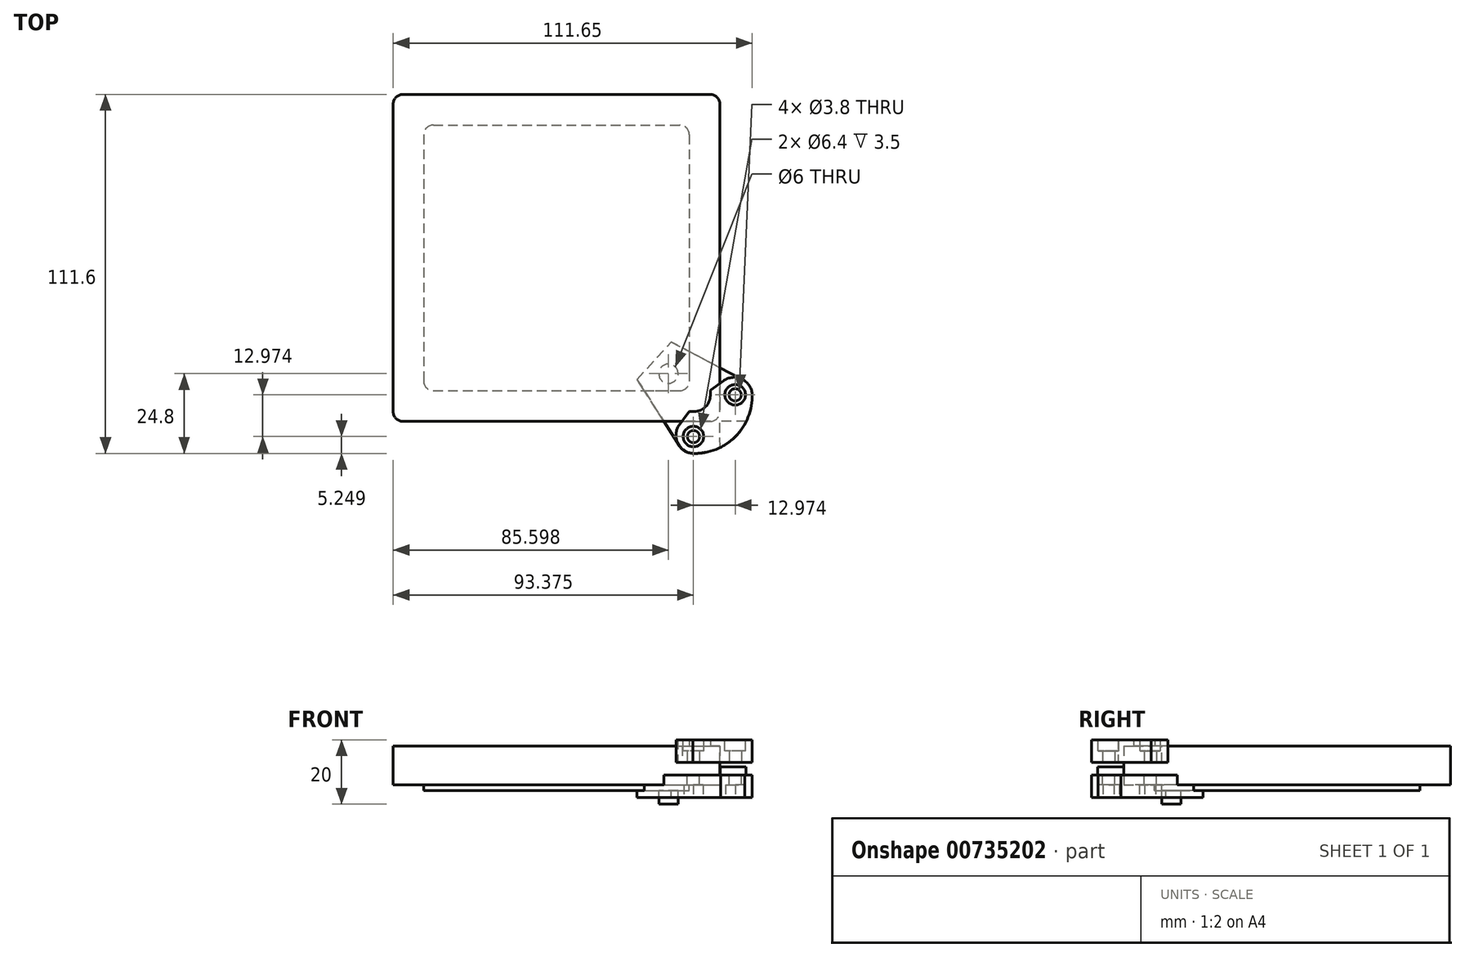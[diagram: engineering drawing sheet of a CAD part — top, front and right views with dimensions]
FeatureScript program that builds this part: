
annotation { "Feature Type Name" : "Feature", "Feature Type Description" : "" }
export const myFeature = defineFeature(function(context is Context, id is Id, definition is map)
    precondition{}
    {
        {
            var Q0;
            Q0=qCreatedBy(makeId("Top.planeOp"),FACE);
            var sketch = newSketch(context, id + "F0", { "sketchPlane" : qUnion([Q0])});
            skLineSegment(sketch, "E0.bottom", {"start": v(-49.2, 52.24) * mm, "end": v(46.4, 52.24) * mm});
            skLineSegment(sketch, "E0.top", {"start": v(-49.2, -49.36) * mm, "end": v(46.4, -49.36) * mm});
            skLineSegment(sketch, "E0.left", {"start": v(-52.2, 49.24) * mm, "end": v(-52.2, -46.36) * mm});
            skLineSegment(sketch, "E0.right", {"start": v(49.4, 49.24) * mm, "end": v(49.4, -46.36) * mm});
            skPoint(sketch, "E1.visualSharp", {"position": v(-52.2, 52.24) * mm});
            skArc(sketch, "E1.filletArc", {"start": v(-49.2, 52.24) * mm, "mid": v(-51.31, 51.36) * mm, "end": v(-52.2, 49.24) * mm});
            skPoint(sketch, "E2.visualSharp", {"position": v(-52.2, -49.36) * mm});
            skArc(sketch, "E2.filletArc", {"start": v(-52.2, -46.36) * mm, "mid": v(-51.31, -48.48) * mm, "end": v(-49.2, -49.36) * mm});
            skPoint(sketch, "E3.visualSharp", {"position": v(49.4, -49.36) * mm});
            skArc(sketch, "E3.filletArc", {"start": v(46.4, -49.36) * mm, "mid": v(48.53, -48.48) * mm, "end": v(49.4, -46.36) * mm});
            skPoint(sketch, "E4.visualSharp", {"position": v(49.4, 52.24) * mm});
            skArc(sketch, "E4.filletArc", {"start": v(49.4, 49.24) * mm, "mid": v(48.53, 51.36) * mm, "end": v(46.4, 52.24) * mm});
            skLineSegment(sketch, "E5.0", {"start": v(-39.7, 42.74) * mm, "end": v(36.9, 42.74) * mm});
            skLineSegment(sketch, "E5.1", {"start": v(-42.7, 39.74) * mm, "end": v(-42.7, -36.86) * mm});
            skLineSegment(sketch, "E5.2", {"start": v(-39.7, -39.86) * mm, "end": v(36.9, -39.86) * mm});
            skLineSegment(sketch, "E5.3", {"start": v(39.9, 39.74) * mm, "end": v(39.9, -36.86) * mm});
            skPoint(sketch, "E6.visualSharp", {"position": v(-42.7, 42.74) * mm});
            skArc(sketch, "E6.filletArc", {"start": v(-39.7, 42.74) * mm, "mid": v(-41.81, 41.86) * mm, "end": v(-42.7, 39.74) * mm});
            skPoint(sketch, "E7.visualSharp", {"position": v(-42.7, -39.86) * mm});
            skArc(sketch, "E7.filletArc", {"start": v(-42.7, -36.86) * mm, "mid": v(-41.81, -38.98) * mm, "end": v(-39.7, -39.86) * mm});
            skPoint(sketch, "E8.visualSharp", {"position": v(39.9, -39.86) * mm});
            skArc(sketch, "E8.filletArc", {"start": v(36.9, -39.86) * mm, "mid": v(39.03, -38.98) * mm, "end": v(39.9, -36.86) * mm});
            skPoint(sketch, "E9.visualSharp", {"position": v(39.9, 42.74) * mm});
            skArc(sketch, "E9.filletArc", {"start": v(39.9, 39.74) * mm, "mid": v(39.03, 41.86) * mm, "end": v(36.9, 42.74) * mm});
            skCircle(sketch, "E10", {"center": v(33.4, -34.56) * mm, "radius": 3 * mm});
            skSolve(sketch);
        }
        {
            var Q0;
            Q0=qSketchRegion(id+"F0",true);
            var Q1;
            Q1=makeQuery(id+"F0.imprint","IMPRINT",FACE,{"disambiguationData":[TD([[makeQuery(id+"F0.imprint","IMPRINT",EDGE,{"derivedFrom":sQuery(id+"F0.wireOp",EDGE,"E5.0")}),-1.0]])]});
            var Q2;
            Q2=makeQuery(id+"F0.imprint","IMPRINT",FACE,{"disambiguationData":[TD([[makeQuery(id+"F0.imprint","IMPRINT",EDGE,{"derivedFrom":sQuery(id+"F0.wireOp",EDGE,"E10")}),1.0]])]});
            extrude(context, id + "F1", {"entities" : qUnion([Q0, Q1, Q2]), "depth" : 12 * mm, "offsetDistance" : 25.4 * mm});
        }
        {
            var Q0;
            Q0=makeQuery(id+"F0.imprint","IMPRINT",FACE,{"disambiguationData":[TD([[makeQuery(id+"F0.imprint","IMPRINT",EDGE,{"derivedFrom":sQuery(id+"F0.wireOp",EDGE,"E5.0")}),-1.0]])]});
            extrude(context, id + "F2", {"entities" : qUnion([Q0]), "operationType" : NewBodyOperationType.ADD, "oppositeDirection" : true, "depth" : 1.8 * mm, "offsetDistance" : 25 * mm});
        }
        {
            var Q0;
            Q0=makeQuery(id+"F2.boolean.opBoolean","SPLIT",FACE,{"disambiguationData":[TD([makeQuery(id+"F2.opExtrude","SWEPT_FACE",FACE,{"disambiguationData":[OSD([sQuery(id+"F0.wireOp",EDGE,"E10")])]})])],"derivedFrom":makeQuery(id+"F1.opExtrude","CAP_FACE",FACE,{"disambiguationData":[OSD([sQuery(id+"F0.wireOp",EDGE,"E0.bottom"),sQuery(id+"F0.wireOp",EDGE,"E0.top"),sQuery(id+"F0.wireOp",EDGE,"E0.left"),sQuery(id+"F0.wireOp",EDGE,"E0.right"),sQuery(id+"F0.wireOp",EDGE,"E1.filletArc"),sQuery(id+"F0.wireOp",EDGE,"E2.filletArc"),sQuery(id+"F0.wireOp",EDGE,"E3.filletArc"),sQuery(id+"F0.wireOp",EDGE,"E4.filletArc")])],"isStart":true})});
            var Q1;
            Q1=sQuery(id+"F0.wireOp",EDGE,"E10");
            extrude(context, id + "F3", {"entities" : qUnion([Q0]), "operationType" : NewBodyOperationType.ADD, "surfaceEntities" : qUnion([Q1]), "depth" : 6 * mm, "offsetDistance" : 25 * mm});
        }
        {
            var Q0;
            Q0=qCreatedBy(makeId("Top.planeOp"),FACE);
            var sketch = newSketch(context, id + "F4", { "sketchPlane" : qUnion([Q0])});
            skLineSegment(sketch, "E11.bottom", {"start": v(56.62, -36.5) * mm, "end": v(34.3, -24.68) * mm});
            skLineSegment(sketch, "E11.top", {"start": v(41.5, -59.36) * mm, "end": v(41.18, -59.36) * mm});
            skLineSegment(sketch, "E11.left", {"start": v(59.4, -41.14) * mm, "end": v(59.4, -41.45) * mm});
            skLineSegment(sketch, "E11.right", {"start": v(23.66, -36.34) * mm, "end": v(36.76, -56.93) * mm});
            skArc(sketch, "E12.filletArc", {"start": v(36.76, -56.93) * mm, "mid": v(38.66, -58.71) * mm, "end": v(41.18, -59.36) * mm});
            skArc(sketch, "E13.filletArc", {"start": v(41.5, -59.36) * mm, "mid": v(54.16, -54.11) * mm, "end": v(59.4, -41.45) * mm});
            skArc(sketch, "E14.filletArc", {"start": v(59.4, -41.14) * mm, "mid": v(58.66, -38.43) * mm, "end": v(56.62, -36.5) * mm});
            skCircle(sketch, "E15", {"center": v(54.16, -41.14) * mm, "radius": 1.9 * mm});
            skCircle(sketch, "E16", {"center": v(41.18, -54.11) * mm, "radius": 1.9 * mm});
            skPoint(sketch, "E17", {"position": v(34.3, -24.68) * mm});
            skPoint(sketch, "E18", {"position": v(23.66, -36.34) * mm});
            skLineSegment(sketch, "E19", {"start": v(34.3, -24.68) * mm, "end": v(23.66, -36.34) * mm});
            skPoint(sketch, "E20", {"position": v(41.18, -59.36) * mm});
            skLineSegment(sketch, "E21", {"start": v(30.2, -46.63) * mm, "end": v(45.46, -30.59) * mm, "construction": true});
            skLineSegment(sketch, "E22", {"start": v(37.83, -38.61) * mm, "end": v(28.98, -30.5) * mm, "construction": true});
            skPoint(sketch, "E23", {"position": v(33.4, -34.56) * mm});
            skLineSegment(sketch, "E24", {"start": v(36.76, -56.93) * mm, "end": v(56.62, -36.5) * mm, "construction": true});
            skLineSegment(sketch, "E25", {"start": v(32.03, -49.5) * mm, "end": v(70.12, -49.5) * mm, "construction": true});
            skLineSegment(sketch, "E26", {"start": v(49.4, -63.01) * mm, "end": v(49.4, -15.8) * mm, "construction": true});
            skLineSegment(sketch, "E27", {"start": v(49.4, -49.5) * mm, "end": v(49.4, -57.52) * mm});
            skLineSegment(sketch, "E28", {"start": v(49.4, -49.5) * mm, "end": v(57.5, -49.5) * mm});
            skEllipticalArc(sketch, "E29", {});
            skLineSegment(sketch, "E30", {"start": v(49.4, -57.5) * mm, "end": v(49.4, -49.5) * mm});
            const initialGuessF4  = {"E29": [0.049408, -0.0494937938059676, 0.7031298044576713, -0.7110615149783577, 0.006693227332354382, 0.010739871215108025, 5.730894756647801, 0.562360824754581]};
            skSetInitialGuess(sketch, initialGuessF4);
            skSolve(sketch);
        }
        {
            var Q0;
            Q0=qSketchRegion(id+"F4",true);
            extrude(context, id + "F5", {"entities" : qUnion([Q0]), "oppositeDirection" : true, "depth" : 7 * mm, "offsetDistance" : 25 * mm});
        }
        {
            var Q0;
            Q0=makeQuery(id+"F5.opExtrude","SWEPT_BODY",BODY,{"disambiguationData":[OSD([sQuery(id+"F4.wireOp",EDGE,"E11.bottom"),sQuery(id+"F4.wireOp",EDGE,"E11.top"),sQuery(id+"F4.wireOp",EDGE,"E11.left"),sQuery(id+"F4.wireOp",EDGE,"E11.right"),sQuery(id+"F4.wireOp",EDGE,"E12.filletArc"),sQuery(id+"F4.wireOp",EDGE,"E13.filletArc"),sQuery(id+"F4.wireOp",EDGE,"E14.filletArc"),sQuery(id+"F4.wireOp",EDGE,"E15"),sQuery(id+"F4.wireOp",EDGE,"E16"),sQuery(id+"F4.wireOp",EDGE,"66c13378-0b8c-4c4a-871f-ac784376b0e9"),sQuery(id+"F4.wireOp",EDGE,"E19")])]});
            transform(context, id + "F6", {"entities" : qUnion([Q0]), "transformType" : TransformType.TRANSLATION_3D, "dx" : 0 * mm, "dy" : 0 * mm, "dz" : 3 * mm, "makeCopy" : false});
        }
        {
            var Q0;
            Q0=makeQuery(id+"F5.opExtrude","CAP_FACE",FACE,{"disambiguationData":[OSD([sQuery(id+"F4.wireOp",EDGE,"E11.bottom"),sQuery(id+"F4.wireOp",EDGE,"E11.top"),sQuery(id+"F4.wireOp",EDGE,"E11.left"),sQuery(id+"F4.wireOp",EDGE,"E11.right"),sQuery(id+"F4.wireOp",EDGE,"E12.filletArc"),sQuery(id+"F4.wireOp",EDGE,"E13.filletArc"),sQuery(id+"F4.wireOp",EDGE,"E14.filletArc"),sQuery(id+"F4.wireOp",EDGE,"E15"),sQuery(id+"F4.wireOp",EDGE,"E16"),sQuery(id+"F4.wireOp",EDGE,"E19")])],"isStart":false});
            var sketch = newSketch(context, id + "F7", { "sketchPlane" : qUnion([Q0])});
            skCircle(sketch, "E31.cCircle", {"center": v(54.16, 41.14) * mm, "radius": 3.4 * mm, "construction": true});
            skLineSegment(sketch, "E31.0", {"start": v(51.2, 42.84) * mm, "end": v(54.16, 44.54) * mm});
            skLineSegment(sketch, "E31.1", {"start": v(54.16, 44.54) * mm, "end": v(57.1, 42.84) * mm});
            skLineSegment(sketch, "E31.2", {"start": v(57.1, 42.84) * mm, "end": v(57.1, 39.43) * mm});
            skLineSegment(sketch, "E31.3", {"start": v(57.1, 39.43) * mm, "end": v(54.16, 37.73) * mm});
            skLineSegment(sketch, "E31.4", {"start": v(54.16, 37.73) * mm, "end": v(51.2, 39.43) * mm});
            skLineSegment(sketch, "E31.5", {"start": v(51.2, 39.43) * mm, "end": v(51.2, 42.84) * mm});
            skCircle(sketch, "E32.cCircle", {"center": v(41.18, 54.11) * mm, "radius": 3.4 * mm, "construction": true});
            skLineSegment(sketch, "E32.0", {"start": v(38.23, 55.81) * mm, "end": v(41.18, 57.52) * mm});
            skLineSegment(sketch, "E32.1", {"start": v(41.18, 57.52) * mm, "end": v(44.13, 55.81) * mm});
            skLineSegment(sketch, "E32.2", {"start": v(44.13, 55.81) * mm, "end": v(44.13, 52.4) * mm});
            skLineSegment(sketch, "E32.3", {"start": v(44.13, 52.4) * mm, "end": v(41.18, 50.7) * mm});
            skLineSegment(sketch, "E32.4", {"start": v(41.18, 50.7) * mm, "end": v(38.23, 52.4) * mm});
            skLineSegment(sketch, "E32.5", {"start": v(38.23, 52.4) * mm, "end": v(38.23, 55.81) * mm});
            skSolve(sketch);
        }
        {
            var Q0;
            Q0=qSketchRegion(id+"F7",true);
            extrude(context, id + "F8", {"entities" : qUnion([Q0]), "operationType" : NewBodyOperationType.REMOVE, "oppositeDirection" : true, "depth" : 4 * mm, "offsetDistance" : 25 * mm});
        }
        {
            var Q0;
            Q0=makeQuery(id+"F1.opExtrude","CAP_FACE",FACE,{"disambiguationData":[OSD([sQuery(id+"F0.wireOp",EDGE,"E0.bottom"),sQuery(id+"F0.wireOp",EDGE,"E0.top"),sQuery(id+"F0.wireOp",EDGE,"E0.left"),sQuery(id+"F0.wireOp",EDGE,"E0.right"),sQuery(id+"F0.wireOp",EDGE,"E1.filletArc"),sQuery(id+"F0.wireOp",EDGE,"E2.filletArc"),sQuery(id+"F0.wireOp",EDGE,"E3.filletArc"),sQuery(id+"F0.wireOp",EDGE,"E4.filletArc")])],"isStart":false});
            var sketch = newSketch(context, id + "F9", { "sketchPlane" : qUnion([Q0])});
            skArc(sketch, "E33.filletArc", {"start": v(41.06, -59.34) * mm, "mid": v(54.24, -54.07) * mm, "end": v(59.45, -40.86) * mm});
            skPoint(sketch, "E34", {"position": v(34.12, -59.33) * mm});
            skCircle(sketch, "E35", {"center": v(54.16, -41.14) * mm, "radius": 1.9 * mm});
            skCircle(sketch, "E36", {"center": v(41.18, -54.11) * mm, "radius": 1.9 * mm});
            skLineSegment(sketch, "E37", {"start": v(50.52, -36.75) * mm, "end": v(46.4, -39.68) * mm});
            skLineSegment(sketch, "E38", {"start": v(46.4, -39.68) * mm, "end": v(46.4, -41.3) * mm});
            skPoint(sketch, "E39.visualSharp", {"position": v(56.89, -32.2) * mm});
            skArc(sketch, "E39.filletArc", {"start": v(59.45, -40.86) * mm, "mid": v(56.17, -36.21) * mm, "end": v(50.52, -36.75) * mm});
            skLineSegment(sketch, "E40", {"start": v(54.24, -54.07) * mm, "end": v(41.55, -41.44) * mm, "construction": true});
            skLineSegment(sketch, "E41.MirrorCS", {"start": v(39.82, -46.31) * mm, "end": v(41.43, -46.3) * mm});
            skLineSegment(sketch, "E42.MirrorCS", {"start": v(36.37, -51.19) * mm, "end": v(39.82, -46.31) * mm});
            skArc(sketch, "E43.MirrorCS", {"start": v(41.06, -59.34) * mm, "mid": v(36.53, -56.52) * mm, "end": v(36.37, -51.19) * mm});
            skPoint(sketch, "E44.visualSharp", {"position": v(46.4, -46.28) * mm});
            skArc(sketch, "E44.filletArc", {"start": v(41.43, -46.3) * mm, "mid": v(44.95, -44.83) * mm, "end": v(46.4, -41.3) * mm});
            skSolve(sketch);
        }
        {
            var Q0;
            Q0=qSketchRegion(id+"F9",true);
            extrude(context, id + "F10", {"entities" : qUnion([Q0]), "depth" : 7 * mm, "offsetDistance" : 25 * mm});
        }
        {
            var Q0;
            Q0=makeQuery(id+"F10.opExtrude","CAP_FACE",FACE,{"disambiguationData":[OSD([sQuery(id+"F9.wireOp",EDGE,"a39b41d0-e7ae-40f5-bbe2-d8dd226e776d.bottom"),sQuery(id+"F9.wireOp",EDGE,"a39b41d0-e7ae-40f5-bbe2-d8dd226e776d.top"),sQuery(id+"F9.wireOp",EDGE,"a39b41d0-e7ae-40f5-bbe2-d8dd226e776d.left"),sQuery(id+"F9.wireOp",EDGE,"a39b41d0-e7ae-40f5-bbe2-d8dd226e776d.right"),sQuery(id+"F9.wireOp",EDGE,"845669e1-6970-4c6b-b3a8-32a38f3c468b.filletArc"),sQuery(id+"F9.wireOp",EDGE,"E33.filletArc"),sQuery(id+"F9.wireOp",EDGE,"ea5769c7-4f24-4bfb-a007-04b614ccd4af.filletArc"),sQuery(id+"F9.wireOp",EDGE,"E35"),sQuery(id+"F9.wireOp",EDGE,"E36")])],"isStart":false});
            var sketch = newSketch(context, id + "F11", { "sketchPlane" : qUnion([Q0])});
            skCircle(sketch, "E45", {"center": v(41.18, -54.11) * mm, "radius": 3.2 * mm});
            skCircle(sketch, "E46", {"center": v(54.16, -41.14) * mm, "radius": 3.2 * mm});
            skSolve(sketch);
        }
        {
            var Q0;
            Q0=qSketchRegion(id+"F11",true);
            extrude(context, id + "F12", {"entities" : qUnion([Q0]), "operationType" : NewBodyOperationType.REMOVE, "oppositeDirection" : true, "depth" : 3.5 * mm, "offsetDistance" : 25 * mm});
        }
        {
            var Q0;
            Q0=makeQuery(id+"F10.opExtrude","SWEPT_BODY",BODY,{"disambiguationData":[OSD([sQuery(id+"F9.wireOp",EDGE,"a39b41d0-e7ae-40f5-bbe2-d8dd226e776d.bottom"),sQuery(id+"F9.wireOp",EDGE,"a39b41d0-e7ae-40f5-bbe2-d8dd226e776d.top"),sQuery(id+"F9.wireOp",EDGE,"a39b41d0-e7ae-40f5-bbe2-d8dd226e776d.left"),sQuery(id+"F9.wireOp",EDGE,"a39b41d0-e7ae-40f5-bbe2-d8dd226e776d.right"),sQuery(id+"F9.wireOp",EDGE,"845669e1-6970-4c6b-b3a8-32a38f3c468b.filletArc"),sQuery(id+"F9.wireOp",EDGE,"E33.filletArc"),sQuery(id+"F9.wireOp",EDGE,"ea5769c7-4f24-4bfb-a007-04b614ccd4af.filletArc"),sQuery(id+"F9.wireOp",EDGE,"E35"),sQuery(id+"F9.wireOp",EDGE,"E36")])]});
            transform(context, id + "F13", {"entities" : qUnion([Q0]), "transformType" : TransformType.TRANSLATION_3D, "dx" : 0 * mm, "dy" : 0 * mm, "dz" : -5 * mm, "makeCopy" : false});
        }
        {
            var Q0;
            Q0=makeQuery(id+"F1.opExtrude","SWEPT_BODY",BODY,{"disambiguationData":[OSD([sQuery(id+"F0.wireOp",EDGE,"E0.bottom"),sQuery(id+"F0.wireOp",EDGE,"E0.top"),sQuery(id+"F0.wireOp",EDGE,"E0.left"),sQuery(id+"F0.wireOp",EDGE,"E0.right"),sQuery(id+"F0.wireOp",EDGE,"E1.filletArc"),sQuery(id+"F0.wireOp",EDGE,"E2.filletArc"),sQuery(id+"F0.wireOp",EDGE,"E3.filletArc"),sQuery(id+"F0.wireOp",EDGE,"E4.filletArc")])]});
            var Q1;
            Q1=makeQuery(id+"F10.opExtrude","SWEPT_BODY",BODY,{"disambiguationData":[OSD([sQuery(id+"F9.wireOp",EDGE,"a39b41d0-e7ae-40f5-bbe2-d8dd226e776d.bottom"),sQuery(id+"F9.wireOp",EDGE,"a39b41d0-e7ae-40f5-bbe2-d8dd226e776d.top"),sQuery(id+"F9.wireOp",EDGE,"a39b41d0-e7ae-40f5-bbe2-d8dd226e776d.left"),sQuery(id+"F9.wireOp",EDGE,"a39b41d0-e7ae-40f5-bbe2-d8dd226e776d.right"),sQuery(id+"F9.wireOp",EDGE,"845669e1-6970-4c6b-b3a8-32a38f3c468b.filletArc"),sQuery(id+"F9.wireOp",EDGE,"E33.filletArc"),sQuery(id+"F9.wireOp",EDGE,"ea5769c7-4f24-4bfb-a007-04b614ccd4af.filletArc"),sQuery(id+"F9.wireOp",EDGE,"E35"),sQuery(id+"F9.wireOp",EDGE,"E36")])]});
            booleanBodies(context, id + "F14", {"operationType" : BooleanOperationType.SUBTRACTION, "tools" : qUnion([Q0]), "targets" : qUnion([Q1]), "keepTools" : true});
        }
        {
            var Q0;
            Q0=makeQuery(id+"F1.opExtrude","SWEPT_BODY",BODY,{"disambiguationData":[OSD([sQuery(id+"F0.wireOp",EDGE,"E0.bottom"),sQuery(id+"F0.wireOp",EDGE,"E0.top"),sQuery(id+"F0.wireOp",EDGE,"E0.left"),sQuery(id+"F0.wireOp",EDGE,"E0.right"),sQuery(id+"F0.wireOp",EDGE,"E1.filletArc"),sQuery(id+"F0.wireOp",EDGE,"E2.filletArc"),sQuery(id+"F0.wireOp",EDGE,"E3.filletArc"),sQuery(id+"F0.wireOp",EDGE,"E4.filletArc")])]});
            var Q1;
            Q1=makeQuery(id+"F5.opExtrude","SWEPT_BODY",BODY,{"disambiguationData":[OSD([sQuery(id+"F4.wireOp",EDGE,"E11.bottom"),sQuery(id+"F4.wireOp",EDGE,"E11.top"),sQuery(id+"F4.wireOp",EDGE,"E11.left"),sQuery(id+"F4.wireOp",EDGE,"E11.right"),sQuery(id+"F4.wireOp",EDGE,"E12.filletArc"),sQuery(id+"F4.wireOp",EDGE,"E13.filletArc"),sQuery(id+"F4.wireOp",EDGE,"E14.filletArc"),sQuery(id+"F4.wireOp",EDGE,"E15"),sQuery(id+"F4.wireOp",EDGE,"E16"),sQuery(id+"F4.wireOp",EDGE,"E19")])]});
            booleanBodies(context, id + "F15", {"operationType" : BooleanOperationType.SUBTRACTION, "tools" : qUnion([Q0]), "targets" : qUnion([Q1]), "keepTools" : true});
        }
        {
            var Q0;
            Q0=makeQuery(id+"F5.opExtrude","CAP_FACE",FACE,{"disambiguationData":[OSD([sQuery(id+"F4.wireOp",EDGE,"E11.bottom"),sQuery(id+"F4.wireOp",EDGE,"E11.top"),sQuery(id+"F4.wireOp",EDGE,"E11.left"),sQuery(id+"F4.wireOp",EDGE,"E11.right"),sQuery(id+"F4.wireOp",EDGE,"E12.filletArc"),sQuery(id+"F4.wireOp",EDGE,"E13.filletArc"),sQuery(id+"F4.wireOp",EDGE,"E14.filletArc"),sQuery(id+"F4.wireOp",EDGE,"E15"),sQuery(id+"F4.wireOp",EDGE,"E16"),sQuery(id+"F4.wireOp",EDGE,"E19"),sQuery(id+"F4.wireOp",EDGE,"E29")])],"isStart":true});
            var sketch = newSketch(context, id + "F16", { "sketchPlane" : qUnion([Q0])});
            skLineSegment(sketch, "E47", {"start": v(32.14, -49.41) * mm, "end": v(70.24, -49.41) * mm, "construction": true});
            skLineSegment(sketch, "E48", {"start": v(49.4, -67.66) * mm, "end": v(49.4, -31.15) * mm, "construction": true});
            skEllipticalArc(sketch, "E49", {});
            skLineSegment(sketch, "E50", {"start": v(49.46, -57.49) * mm, "end": v(49.4, -49.36) * mm});
            skLineSegment(sketch, "E51", {"start": v(57.57, -49.41) * mm, "end": v(49.4, -49.36) * mm});
            const initialGuessF16  = {"E49": [0.049408, -0.04936, 0.7031298044576713, -0.7110615149783577, 0.006804975713047634, 0.010919181308363177, 5.7363346115275835, 0.5568305108967264]};
            skSetInitialGuess(sketch, initialGuessF16);
            skSolve(sketch);
        }
        {
            var Q0;
            Q0=qSketchRegion(id+"F16",true);
            extrude(context, id + "F17", {"entities" : qUnion([Q0]), "operationType" : NewBodyOperationType.ADD, "depth" : 2.5 * mm, "offsetDistance" : 25 * mm});
        }
    });
